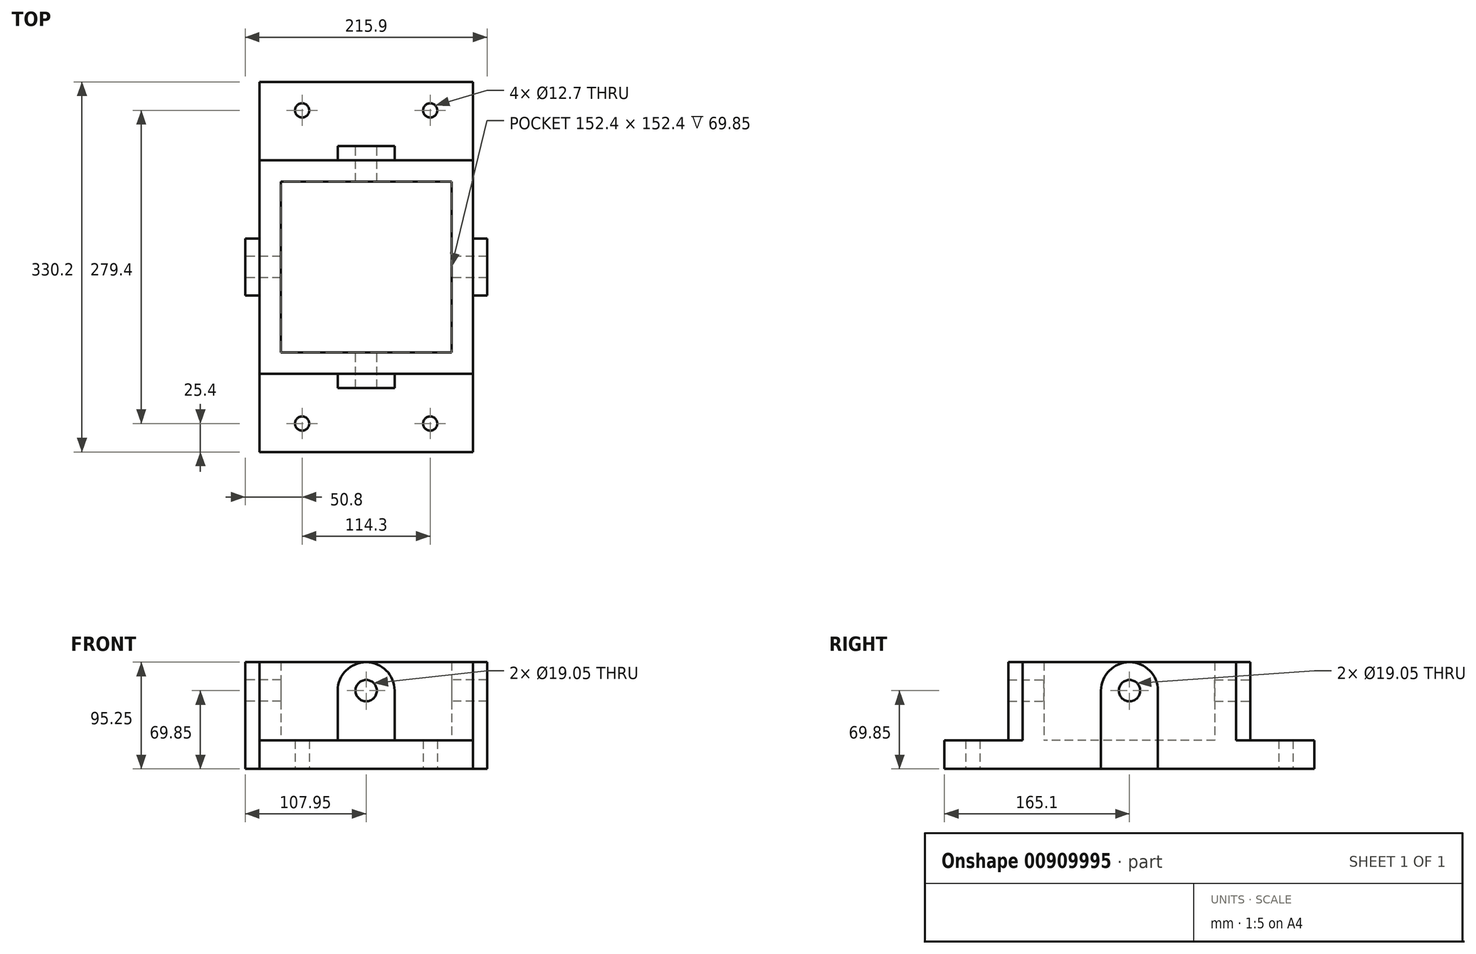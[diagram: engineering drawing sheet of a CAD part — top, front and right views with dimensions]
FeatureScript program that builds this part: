
annotation { "Feature Type Name" : "Feature", "Feature Type Description" : "" }
export const myFeature = defineFeature(function(context is Context, id is Id, definition is map)
    precondition{}
    {
        {
            var Q0;
            Q0=qCreatedBy(makeId("Front.planeOp"),FACE);
            var sketch = newSketch(context, id + "F0", { "sketchPlane" : qUnion([Q0])});
            skLineSegment(sketch, "E0.bottom", {"start": v(-95.25, 25.4) * mm, "end": v(95.25, 25.4) * mm});
            skLineSegment(sketch, "E0.top", {"start": v(-95.25, 0) * mm, "end": v(95.25, 0) * mm});
            skLineSegment(sketch, "E0.left", {"start": v(-95.25, 25.4) * mm, "end": v(-95.25, 0) * mm});
            skLineSegment(sketch, "E0.right", {"start": v(95.25, 25.4) * mm, "end": v(95.25, 0) * mm});
            skLineSegment(sketch, "E1", {"start": v(-95.25, 25.4) * mm, "end": v(-95.25, 95.25) * mm});
            skLineSegment(sketch, "E2", {"start": v(-95.25, 95.25) * mm, "end": v(-76.2, 95.25) * mm});
            skLineSegment(sketch, "E3", {"start": v(95.25, 95.25) * mm, "end": v(95.25, 25.4) * mm});
            skLineSegment(sketch, "E4", {"start": v(-76.2, 95.25) * mm, "end": v(-76.2, 25.4) * mm});
            skLineSegment(sketch, "E5", {"start": v(76.2, 95.25) * mm, "end": v(76.2, 95.25) * mm});
            skLineSegment(sketch, "E6", {"start": v(-76.2, 95.25) * mm, "end": v(76.2, 95.25) * mm});
            skLineSegment(sketch, "E7", {"start": v(76.2, 95.25) * mm, "end": v(76.2, 25.4) * mm});
            skLineSegment(sketch, "E8", {"start": v(76.2, 95.25) * mm, "end": v(95.25, 95.25) * mm});
            skPoint(sketch, "E9", {"position": v(0, 0) * mm});
            skArc(sketch, "E10", {"start": v(25.4, 69.85) * mm, "mid": v(0, 95.25) * mm, "end": v(-25.4, 69.85) * mm});
            skLineSegment(sketch, "E11", {"start": v(-25.4, 69.85) * mm, "end": v(-25.4, 25.4) * mm});
            skLineSegment(sketch, "E12", {"start": v(25.4, 69.85) * mm, "end": v(25.4, 25.4) * mm});
            skCircle(sketch, "E13", {"center": v(0, 69.85) * mm, "radius": 9.53 * mm});
            skSolve(sketch);
        }
        {
            var Q0;
            Q0=makeQuery(id+"F0.imprint","IMPRINT",FACE,{"disambiguationData":[TD([[makeQuery(id+"F0.imprint","IMPRINT",EDGE,{"derivedFrom":sQuery(id+"F0.wireOp",EDGE,"E0.top")}),1.0]])]});
            extrude(context, id + "F1", {"entities" : qUnion([Q0]), "depth" : 330.2 * mm, "offsetDistance" : 25 * mm, "symmetric" : true});
        }
        {
            var Q0;
            {var subQ0=sQuery(id+"F0.wireOp",EDGE,"E1");Q0=makeQuery(id+"F0.imprint","IMPRINT",FACE,{"disambiguationData":[TD([[makeQuery(id+"F0.imprint","IMPRINT",EDGE,{"derivedFrom":subQ0}),-1.0]])]});}
            var Q1;
            {var subQ4=sQuery(id+"F0.wireOp",EDGE,"E4");Q1=makeQuery(id+"F0.imprint","IMPRINT",FACE,{"disambiguationData":[TD([[makeQuery(id+"F0.imprint","IMPRINT",EDGE,{"derivedFrom":subQ4}),1.0]])]});}
            var Q2;
            {var subQ0=sQuery(id+"F0.wireOp",EDGE,"E11");Q2=makeQuery(id+"F0.imprint","IMPRINT",FACE,{"disambiguationData":[TD([[makeQuery(id+"F0.imprint","IMPRINT",EDGE,{"derivedFrom":subQ0}),1.0]])]});}
            var Q3;
            {var subQ4=sQuery(id+"F0.wireOp",EDGE,"E7");Q3=makeQuery(id+"F0.imprint","IMPRINT",FACE,{"disambiguationData":[TD([[makeQuery(id+"F0.imprint","IMPRINT",EDGE,{"derivedFrom":subQ4}),-1.0]])]});}
            var Q4;
            {var subQ0=sQuery(id+"F0.wireOp",EDGE,"E3");Q4=makeQuery(id+"F0.imprint","IMPRINT",FACE,{"disambiguationData":[TD([[makeQuery(id+"F0.imprint","IMPRINT",EDGE,{"derivedFrom":subQ0}),-1.0]])]});}
            extrude(context, id + "F2", {"entities" : qUnion([Q0, Q1, Q2, Q3, Q4]), "operationType" : NewBodyOperationType.ADD, "depth" : 190.5 * mm, "offsetDistance" : 25 * mm, "symmetric" : true});
        }
        {
            var Q0;
            Q0=makeQuery(id+"F0.imprint","IMPRINT",FACE,{"disambiguationData":[TD([[makeQuery(id+"F0.imprint","IMPRINT",EDGE,{"derivedFrom":sQuery(id+"F0.wireOp",EDGE,"E10")}),1.0]])]});
            extrude(context, id + "F3", {"entities" : qUnion([Q0]), "operationType" : NewBodyOperationType.ADD, "depth" : 215.9 * mm, "offsetDistance" : 25 * mm, "symmetric" : true});
        }
        {
            var Q0;
            Q0=qCreatedBy(makeId("Right.planeOp"),FACE);
            var sketch = newSketch(context, id + "F4", { "sketchPlane" : qUnion([Q0])});
            skCircle(sketch, "E14", {"center": v(0, 69.85) * mm, "radius": 9.53 * mm});
            skArc(sketch, "E15", {"start": v(25.4, 69.85) * mm, "mid": v(0, 95.25) * mm, "end": v(-25.4, 69.85) * mm});
            skLineSegment(sketch, "E16", {"start": v(-25.4, 69.85) * mm, "end": v(-25.4, 0) * mm});
            skLineSegment(sketch, "E17", {"start": v(-25.4, 0) * mm, "end": v(25.4, 0) * mm});
            skLineSegment(sketch, "E18", {"start": v(25.4, 0) * mm, "end": v(25.4, 69.85) * mm});
            skSolve(sketch);
        }
        {
            var Q0;
            Q0=makeQuery(id+"F4.imprint","IMPRINT",FACE,{"disambiguationData":[TD([[makeQuery(id+"F4.imprint","IMPRINT",EDGE,{"derivedFrom":sQuery(id+"F4.wireOp",EDGE,"E14")}),-1.0]])]});
            extrude(context, id + "F5", {"entities" : qUnion([Q0]), "operationType" : NewBodyOperationType.ADD, "depth" : 215.9 * mm, "offsetDistance" : 25 * mm, "symmetric" : true});
        }
        {
            var Q0;
            {var subQ0=sQuery(id+"F0.wireOp",EDGE,"E4");Q0=makeQuery(id+"F0.imprint","IMPRINT",FACE,{"disambiguationData":[TD([[makeQuery(id+"F0.imprint","IMPRINT",EDGE,{"derivedFrom":subQ0}),1.0]])]});}
            var Q1;
            Q1=makeQuery(id+"F0.imprint","IMPRINT",FACE,{"disambiguationData":[TD([[makeQuery(id+"F0.imprint","IMPRINT",EDGE,{"derivedFrom":sQuery(id+"F0.wireOp",EDGE,"E10")}),1.0]])]});
            var Q2;
            {var subQ4=sQuery(id+"F0.wireOp",EDGE,"E7");Q2=makeQuery(id+"F0.imprint","IMPRINT",FACE,{"disambiguationData":[TD([[makeQuery(id+"F0.imprint","IMPRINT",EDGE,{"derivedFrom":subQ4}),-1.0]])]});}
            var Q3;
            Q3=makeQuery(id+"F0.imprint","IMPRINT",FACE,{"disambiguationData":[TD([[makeQuery(id+"F0.imprint","IMPRINT",EDGE,{"derivedFrom":sQuery(id+"F0.wireOp",EDGE,"E13")}),1.0]])]});
            extrude(context, id + "F6", {"entities" : qUnion([Q0, Q1, Q2, Q3]), "operationType" : NewBodyOperationType.REMOVE, "oppositeDirection" : true, "depth" : 152.4 * mm, "offsetDistance" : 25 * mm, "symmetric" : true});
        }
        {
            var Q0;
            Q0=makeQuery(id+"F4.imprint","IMPRINT",FACE,{"disambiguationData":[TD([[makeQuery(id+"F4.imprint","IMPRINT",EDGE,{"derivedFrom":sQuery(id+"F4.wireOp",EDGE,"E14")}),1.0]])]});
            extrude(context, id + "F7", {"entities" : qUnion([Q0]), "operationType" : NewBodyOperationType.REMOVE, "oppositeDirection" : true, "depth" : 203.2 * mm, "offsetDistance" : 25 * mm, "symmetric" : true});
        }
        {
            var Q0;
            Q0=makeQuery(id+"F1.opExtrude","SWEPT_FACE",FACE,{"disambiguationData":[OSD([sQuery(id+"F0.wireOp",EDGE,"E0.top")])]});
            var sketch = newSketch(context, id + "F8", { "sketchPlane" : qUnion([Q0])});
            skLineSegment(sketch, "E19.bottom", {"start": v(-57.15, 139.7) * mm, "end": v(57.15, 139.7) * mm, "construction": true});
            skLineSegment(sketch, "E19.top", {"start": v(-57.15, -139.7) * mm, "end": v(57.15, -139.7) * mm, "construction": true});
            skLineSegment(sketch, "E19.left", {"start": v(-57.15, 139.7) * mm, "end": v(-57.15, -139.7) * mm, "construction": true});
            skLineSegment(sketch, "E19.right", {"start": v(57.15, 139.7) * mm, "end": v(57.15, -139.7) * mm, "construction": true});
            skCircle(sketch, "E20", {"center": v(-57.15, 139.7) * mm, "radius": 6.35 * mm});
            skCircle(sketch, "E21", {"center": v(57.15, 139.7) * mm, "radius": 6.35 * mm});
            skCircle(sketch, "E22", {"center": v(-57.15, -139.7) * mm, "radius": 6.35 * mm});
            skCircle(sketch, "E23", {"center": v(57.15, -139.7) * mm, "radius": 6.35 * mm});
            skLineSegment(sketch, "E24", {"start": v(0, 139.7) * mm, "end": v(0, -139.7) * mm, "construction": true});
            skLineSegment(sketch, "E25", {"start": v(-57.15, 0) * mm, "end": v(57.15, 0) * mm, "construction": true});
            skSolve(sketch);
        }
        {
            var Q0;
            Q0=makeQuery(id+"F8.imprint","IMPRINT",FACE,{"disambiguationData":[TD([[makeQuery(id+"F8.imprint","IMPRINT",EDGE,{"derivedFrom":sQuery(id+"F8.wireOp",EDGE,"E20")}),1.0]])]});
            var Q1;
            Q1=makeQuery(id+"F8.imprint","IMPRINT",FACE,{"disambiguationData":[TD([[makeQuery(id+"F8.imprint","IMPRINT",EDGE,{"derivedFrom":sQuery(id+"F8.wireOp",EDGE,"E21")}),1.0]])]});
            var Q2;
            Q2=makeQuery(id+"F8.imprint","IMPRINT",FACE,{"disambiguationData":[TD([[makeQuery(id+"F8.imprint","IMPRINT",EDGE,{"derivedFrom":sQuery(id+"F8.wireOp",EDGE,"E23")}),1.0]])]});
            var Q3;
            Q3=makeQuery(id+"F8.imprint","IMPRINT",FACE,{"disambiguationData":[TD([[makeQuery(id+"F8.imprint","IMPRINT",EDGE,{"derivedFrom":sQuery(id+"F8.wireOp",EDGE,"E22")}),1.0]])]});
            extrude(context, id + "F9", {"entities" : qUnion([Q0, Q1, Q2, Q3]), "operationType" : NewBodyOperationType.REMOVE, "endBound" : BoundingType.THROUGH_ALL, "oppositeDirection" : true, "depth" : 25 * mm, "offsetDistance" : 25 * mm});
        }
    });
